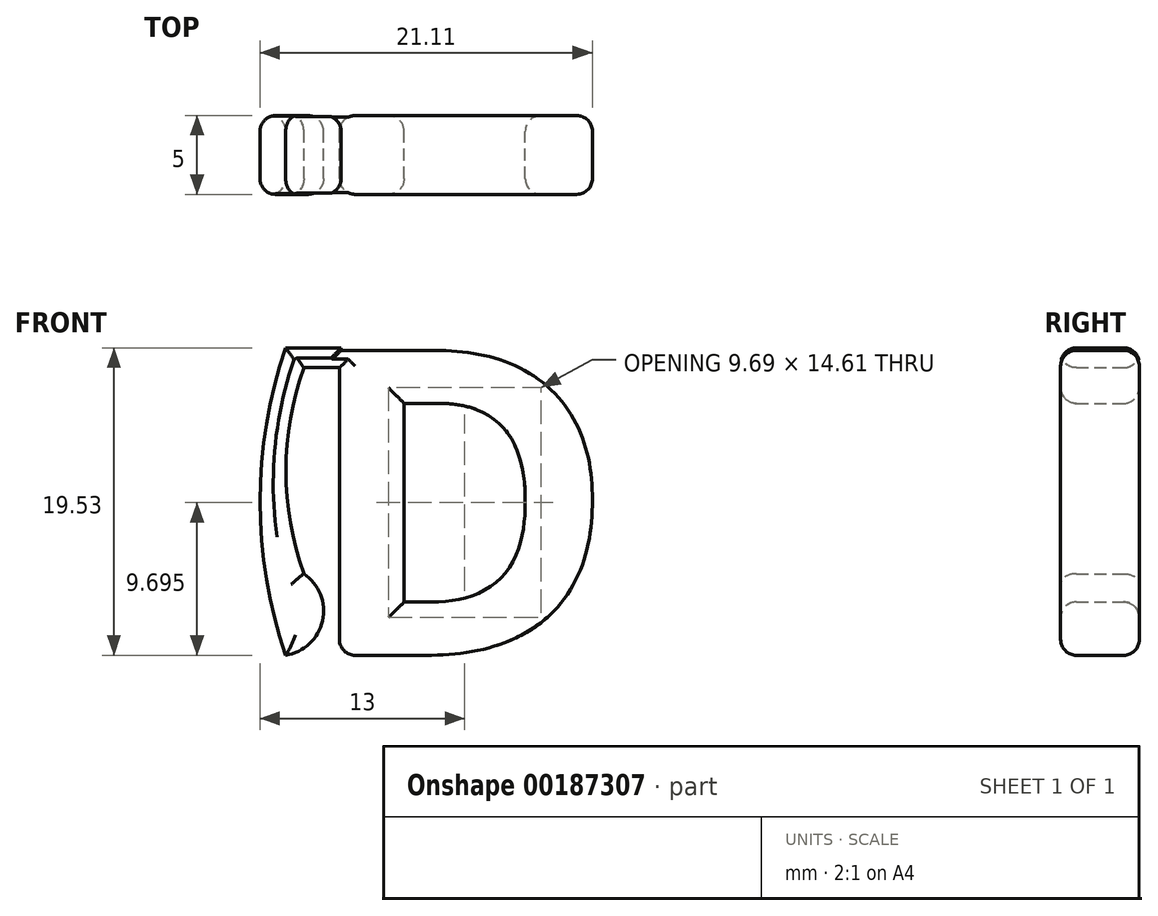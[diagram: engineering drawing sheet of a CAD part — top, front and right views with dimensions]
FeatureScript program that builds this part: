
annotation { "Feature Type Name" : "Feature", "Feature Type Description" : "" }
export const myFeature = defineFeature(function(context is Context, id is Id, definition is map)
    precondition{}
    {
        {
            var Q0;
            Q0=qCreatedBy(makeId("Front.planeOp"),FACE);
            var sketch = newSketch(context, id + "F0", { "sketchPlane" : qUnion([Q0])});
            skLineSegment(sketch, "E0", {"start": v(0, 19.53) * mm, "end": v(3.52, 19.53) * mm});
            skLineSegment(sketch, "E1", {"start": v(3.52, 19.53) * mm, "end": v(3.52, 18.27) * mm});
            skLineSegment(sketch, "E2", {"start": v(3.52, 18.27) * mm, "end": v(1.16, 18.27) * mm});
            skArc(sketch, "E3", {"start": v(0, 0) * mm, "mid": v(2.34, 2.2) * mm, "end": v(1.16, 5.18) * mm});
            skText(sketch, "E4", { "text": "D", "fontName": "OpenSans-Bold.ttf"});
            skArc(sketch, "E5", {"start": v(1.16, 18.27) * mm, "mid": v(0.02, 11.72) * mm, "end": v(1.16, 5.18) * mm});
            skArc(sketch, "E6", {"start": v(0, 19.53) * mm, "mid": v(-1.63, 9.76) * mm, "end": v(0, 0) * mm});
            const initialGuessF0  = {"E4": [0.00098, 0, 1, 0, 0.01953]};
            skSetInitialGuess(sketch, initialGuessF0);
            skSolve(sketch);
        }
        {
            var Q0;
            Q0=qSketchRegion(id+"F0",true);
            extrude(context, id + "F1", {"entities" : qUnion([Q0]), "depth" : 5 * mm});
        }
        {
            var Q0;
            Q0=makeQuery(id+"F1.opExtrude","CAP_FACE",FACE,{"disambiguationData":[OSD([sQuery(id+"F0.wireOp",EDGE,"be7xAEPO-sKVT-0Ak3-rtqd-BYsUKJHZuXb5"),sQuery(id+"F0.wireOp",EDGE,"E0"),sQuery(id+"F0.wireOp",EDGE,"E1"),sQuery(id+"F0.wireOp",EDGE,"E2"),sQuery(id+"F0.wireOp",EDGE,"7xSTVDnR-abPq-wSY4-ofMi-LYckJfvl9Wuv"),sQuery(id+"F0.wireOp",EDGE,"E3"),sQuery(id+"F0.wireOp",EDGE,"E4.sketch_text.stroke-0"),sQuery(id+"F0.wireOp",EDGE,"E4.sketch_text.stroke-1"),sQuery(id+"F0.wireOp",EDGE,"E4.sketch_text.stroke-2"),sQuery(id+"F0.wireOp",EDGE,"E4.sketch_text.stroke-3"),sQuery(id+"F0.wireOp",EDGE,"E4.sketch_text.stroke-4"),sQuery(id+"F0.wireOp",EDGE,"E4.sketch_text.stroke-5"),sQuery(id+"F0.wireOp",EDGE,"E4.sketch_text.stroke-6"),sQuery(id+"F0.wireOp",EDGE,"E4.sketch_text.stroke-7"),sQuery(id+"F0.wireOp",EDGE,"E4.sketch_text.stroke-8"),sQuery(id+"F0.wireOp",EDGE,"E4.sketch_text.stroke-9")])],"isStart":false});
            var Q1;
            Q1=makeQuery(id+"F1.opExtrude","CAP_FACE",FACE,{"disambiguationData":[OSD([sQuery(id+"F0.wireOp",EDGE,"be7xAEPO-sKVT-0Ak3-rtqd-BYsUKJHZuXb5"),sQuery(id+"F0.wireOp",EDGE,"E0"),sQuery(id+"F0.wireOp",EDGE,"E1"),sQuery(id+"F0.wireOp",EDGE,"E2"),sQuery(id+"F0.wireOp",EDGE,"7xSTVDnR-abPq-wSY4-ofMi-LYckJfvl9Wuv"),sQuery(id+"F0.wireOp",EDGE,"E3"),sQuery(id+"F0.wireOp",EDGE,"E4.sketch_text.stroke-0"),sQuery(id+"F0.wireOp",EDGE,"E4.sketch_text.stroke-1"),sQuery(id+"F0.wireOp",EDGE,"E4.sketch_text.stroke-2"),sQuery(id+"F0.wireOp",EDGE,"E4.sketch_text.stroke-3"),sQuery(id+"F0.wireOp",EDGE,"E4.sketch_text.stroke-4"),sQuery(id+"F0.wireOp",EDGE,"E4.sketch_text.stroke-5"),sQuery(id+"F0.wireOp",EDGE,"E4.sketch_text.stroke-6"),sQuery(id+"F0.wireOp",EDGE,"E4.sketch_text.stroke-7"),sQuery(id+"F0.wireOp",EDGE,"E4.sketch_text.stroke-8"),sQuery(id+"F0.wireOp",EDGE,"E4.sketch_text.stroke-9")])],"isStart":true});
            fillet(context, id + "F2", {"entities" : qUnion([Q0, Q1]), "radius" : 1 * mm, "tangentPropagation" : true, "allowEdgeOverflow" : false});
        }
        {
            var Q0;
            Q0=makeQuery(id+"F1.opExtrude","SWEPT_EDGE",EDGE,{"disambiguationData":[OSD([sQuery(id+"F0.wireOp",EDGE,"E4.sketch_text.stroke-2"),sQuery(id+"F0.wireOp",EDGE,"E4.sketch_text.stroke-3")])]});
            fillet(context, id + "F3", {"entities" : qUnion([Q0]), "radius" : 1 * mm, "tangentPropagation" : true, "allowEdgeOverflow" : false});
        }
    });
